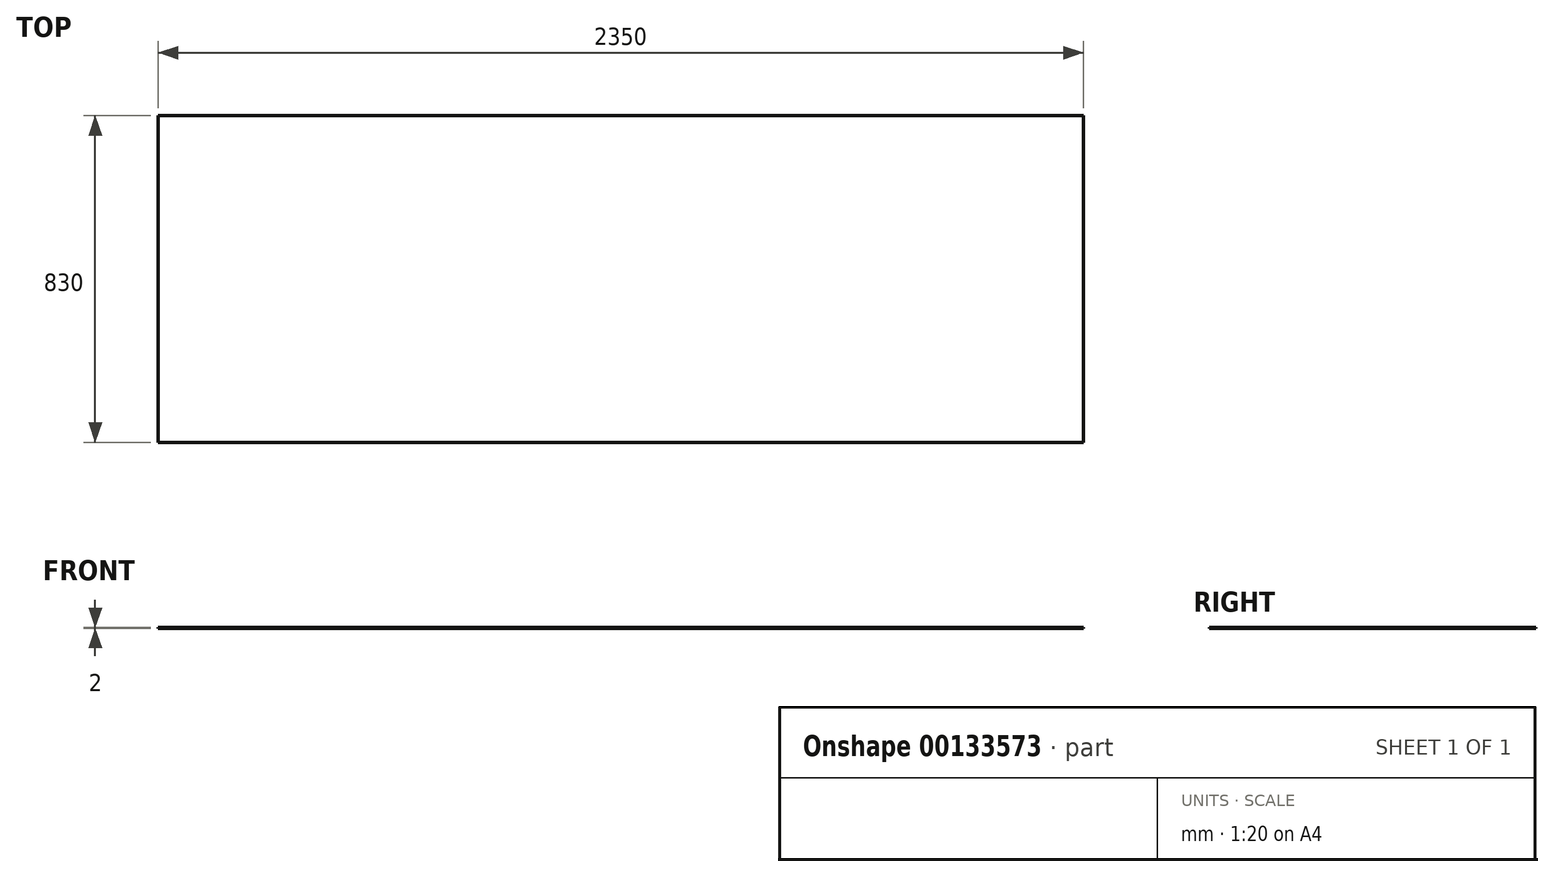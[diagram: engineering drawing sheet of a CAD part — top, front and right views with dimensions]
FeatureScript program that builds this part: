
annotation { "Feature Type Name" : "Feature", "Feature Type Description" : "" }
export const myFeature = defineFeature(function(context is Context, id is Id, definition is map)
    precondition{}
    {
        {
            var Q0;
            Q0=qCreatedBy(makeId("Top.planeOp"),FACE);
            var sketch = newSketch(context, id + "F0", { "sketchPlane" : qUnion([Q0])});
            skLineSegment(sketch, "E0.bottom", {"start": v(0, 0) * mm, "end": v(2350, 0) * mm});
            skLineSegment(sketch, "E0.top", {"start": v(0, -830) * mm, "end": v(2350, -830) * mm});
            skLineSegment(sketch, "E0.left", {"start": v(0, 0) * mm, "end": v(0, -830) * mm});
            skLineSegment(sketch, "E0.right", {"start": v(2350, 0) * mm, "end": v(2350, -830) * mm});
            skSolve(sketch);
        }
        {
            var Q0;
            Q0=makeQuery(id+"F0.imprint","IMPRINT",FACE,{"disambiguationData":[TD([[makeQuery(id+"F0.imprint","IMPRINT",EDGE,{"derivedFrom":sQuery(id+"F0.wireOp",EDGE,"E0.bottom")}),-1.0]])]});
            extrude(context, id + "F1", {"entities" : qUnion([Q0]), "depth" : 2 * mm});
        }
    });
